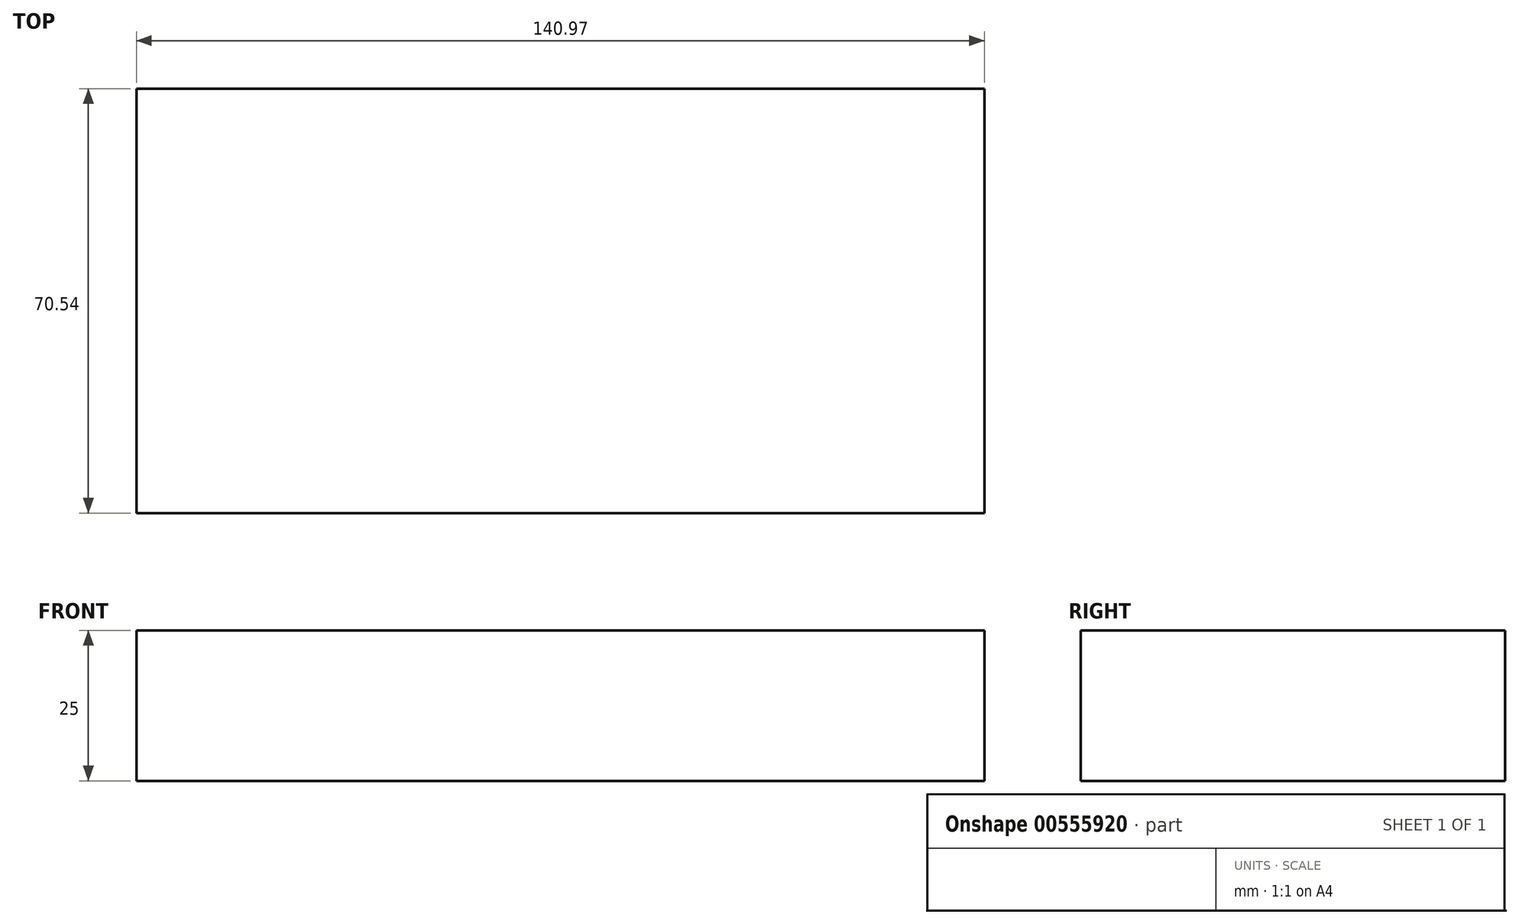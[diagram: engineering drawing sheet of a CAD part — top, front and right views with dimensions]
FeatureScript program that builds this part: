
annotation { "Feature Type Name" : "Feature", "Feature Type Description" : "" }
export const myFeature = defineFeature(function(context is Context, id is Id, definition is map)
    precondition{}
    {
        {
            var Q0;
            Q0=qCreatedBy(makeId("Top.planeOp"),FACE);
            var sketch = newSketch(context, id + "F0", { "sketchPlane" : qUnion([Q0])});
            skLineSegment(sketch, "E0.bottom", {"start": v(70.77, 0) * mm, "end": v(-70.2, 0) * mm});
            skLineSegment(sketch, "E0.top", {"start": v(70.77, 70.54) * mm, "end": v(-70.2, 70.54) * mm});
            skLineSegment(sketch, "E0.left", {"start": v(70.77, 0) * mm, "end": v(70.77, 70.54) * mm});
            skLineSegment(sketch, "E0.right", {"start": v(-70.2, 0) * mm, "end": v(-70.2, 70.54) * mm});
            skSolve(sketch);
        }
        {
            var Q0;
            Q0=makeQuery(id+"F0.imprint","IMPRINT",FACE,{"disambiguationData":[TD([[makeQuery(id+"F0.imprint","IMPRINT",EDGE,{"derivedFrom":sQuery(id+"F0.wireOp",EDGE,"E0.bottom")}),-1.0]])]});
            extrude(context, id + "F1", {"entities" : qUnion([Q0]), "depth" : 10 * mm, "offsetDistance" : 25 * mm});
        }
        {
            var Q0;
            Q0=makeQuery(id+"F1.opExtrude","CAP_FACE",FACE,{"disambiguationData":[OSD([sQuery(id+"F0.wireOp",EDGE,"E0.bottom"),sQuery(id+"F0.wireOp",EDGE,"E0.top"),sQuery(id+"F0.wireOp",EDGE,"E0.left"),sQuery(id+"F0.wireOp",EDGE,"E0.right")])],"isStart":false});
            extrude(context, id + "F2", {"entities" : qUnion([Q0]), "operationType" : NewBodyOperationType.ADD, "depth" : 8.5 * mm, "offsetDistance" : 25 * mm});
        }
        {
            var Q0;
            Q0=makeQuery(id+"F2.opExtrude","CAP_FACE",FACE,{"disambiguationData":[OSD([sQuery(id+"F0.wireOp",EDGE,"E0.bottom"),sQuery(id+"F0.wireOp",EDGE,"E0.top"),sQuery(id+"F0.wireOp",EDGE,"E0.left"),sQuery(id+"F0.wireOp",EDGE,"E0.right")])],"isStart":false});
            extrude(context, id + "F3", {"entities" : qUnion([Q0]), "operationType" : NewBodyOperationType.ADD, "depth" : -25 * mm, "offsetDistance" : 25 * mm});
        }
    });
